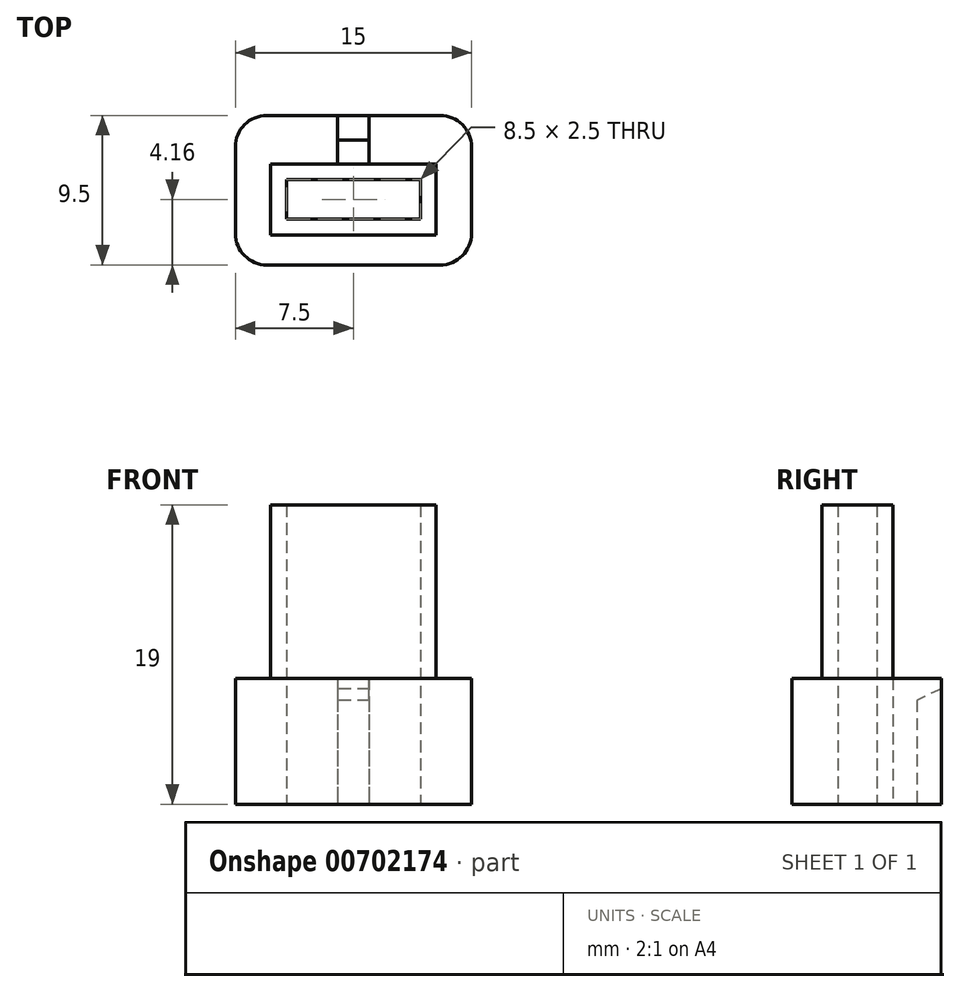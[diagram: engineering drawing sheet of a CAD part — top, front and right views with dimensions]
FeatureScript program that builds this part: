
annotation { "Feature Type Name" : "Feature", "Feature Type Description" : "" }
export const myFeature = defineFeature(function(context is Context, id is Id, definition is map)
    precondition{}
    {
        {
            var Q0;
            Q0=qCreatedBy(makeId("Top.planeOp"),FACE);
            var sketch = newSketch(context, id + "F0", { "sketchPlane" : qUnion([Q0])});
            skLineSegment(sketch, "E0.bottom", {"start": v(4.25, -1.25) * mm, "end": v(-4.25, -1.25) * mm});
            skLineSegment(sketch, "E0.top", {"start": v(4.25, 1.25) * mm, "end": v(-4.25, 1.25) * mm});
            skLineSegment(sketch, "E0.left", {"start": v(4.25, -1.25) * mm, "end": v(4.25, 1.25) * mm});
            skLineSegment(sketch, "E0.right", {"start": v(-4.25, -1.25) * mm, "end": v(-4.25, 1.25) * mm});
            skPoint(sketch, "E0.middle", {"position": v(0, 0) * mm});
            skLineSegment(sketch, "E1.bottom", {"start": v(5.25, -2.25) * mm, "end": v(-5.25, -2.25) * mm});
            skLineSegment(sketch, "E1.top", {"start": v(5.25, 2.25) * mm, "end": v(-5.25, 2.25) * mm});
            skLineSegment(sketch, "E1.left", {"start": v(5.25, -2.25) * mm, "end": v(5.25, 2.25) * mm});
            skLineSegment(sketch, "E1.right", {"start": v(-5.25, -2.25) * mm, "end": v(-5.25, 2.25) * mm});
            skLineSegment(sketch, "E2.bottom", {"start": v(1, 2.25) * mm, "end": v(-1, 2.25) * mm});
            skLineSegment(sketch, "E2.top", {"start": v(1, 3.76) * mm, "end": v(-1, 3.76) * mm});
            skLineSegment(sketch, "E2.left", {"start": v(1, 2.25) * mm, "end": v(1, 3.76) * mm});
            skLineSegment(sketch, "E2.right", {"start": v(-1, 2.25) * mm, "end": v(-1, 3.76) * mm});
            skPoint(sketch, "E2.middle", {"position": v(0, 3) * mm});
            skPoint(sketch, "E2.middle.positionSnap0", {"position": v(0, 2.25) * mm});
            skPoint(sketch, "E2.centerSnap0", {"position": v(0, 2.25) * mm});
            skLineSegment(sketch, "E3.bottom", {"start": v(7.5, -4.16) * mm, "end": v(-7.5, -4.16) * mm});
            skLineSegment(sketch, "E3.top", {"start": v(7.5, 5.34) * mm, "end": v(-7.5, 5.34) * mm});
            skLineSegment(sketch, "E3.left", {"start": v(7.5, -4.16) * mm, "end": v(7.5, 5.34) * mm});
            skLineSegment(sketch, "E3.right", {"start": v(-7.5, -4.16) * mm, "end": v(-7.5, 5.34) * mm});
            skPoint(sketch, "E3.middle", {"position": v(0, 0.59) * mm});
            skSolve(sketch);
        }
        {
            var Q0;
            Q0=makeQuery(id+"F0.imprint","IMPRINT",FACE,{"disambiguationData":[TD([[makeQuery(id+"F0.imprint","IMPRINT",EDGE,{"derivedFrom":sQuery(id+"F0.wireOp",EDGE,"E0.bottom")}),1.0]])]});
            var Q1;
            Q1=makeQuery(id+"F0.imprint","IMPRINT",FACE,{"disambiguationData":[TD([[makeQuery(id+"F0.imprint","IMPRINT",EDGE,{"derivedFrom":sQuery(id+"F0.wireOp",EDGE,"E2.bottom")}),-1.0]])]});
            extrude(context, id + "F1", {"entities" : qUnion([Q0, Q1]), "depth" : 19 * mm, "offsetDistance" : 25 * mm});
        }
        {
            var Q0;
            Q0=makeQuery(id+"F0.imprint","IMPRINT",FACE,{"disambiguationData":[TD([[makeQuery(id+"F0.imprint","IMPRINT",EDGE,{"derivedFrom":sQuery(id+"F0.wireOp",EDGE,"E1.bottom")}),1.0]])]});
            extrude(context, id + "F2", {"entities" : qUnion([Q0]), "operationType" : NewBodyOperationType.ADD, "depth" : 8 * mm, "offsetDistance" : 25 * mm});
        }
        {
            var Q0;
            Q0=makeQuery(id+"F2.opExtrude","SWEPT_EDGE",EDGE,{"disambiguationData":[OSD([sQuery(id+"F0.wireOp",EDGE,"E3.bottom"),sQuery(id+"F0.wireOp",EDGE,"E3.right")])]});
            var Q1;
            Q1=makeQuery(id+"F2.opExtrude","SWEPT_EDGE",EDGE,{"disambiguationData":[OSD([sQuery(id+"F0.wireOp",EDGE,"E3.bottom"),sQuery(id+"F0.wireOp",EDGE,"E3.left")])]});
            var Q2;
            Q2=makeQuery(id+"F2.opExtrude","SWEPT_EDGE",EDGE,{"disambiguationData":[OSD([sQuery(id+"F0.wireOp",EDGE,"E3.top"),sQuery(id+"F0.wireOp",EDGE,"E3.left")])]});
            var Q3;
            Q3=makeQuery(id+"F2.opExtrude","SWEPT_EDGE",EDGE,{"disambiguationData":[OSD([sQuery(id+"F0.wireOp",EDGE,"E3.top"),sQuery(id+"F0.wireOp",EDGE,"E3.right")])]});
            fillet(context, id + "F3", {"entities" : qUnion([Q0, Q1, Q2, Q3]), "radius" : 2 * mm, "tangentPropagation" : true, "allowEdgeOverflow" : false});
        }
        {
            var Q0;
            Q0=makeQuery(id+"F2.opExtrude","CAP_EDGE",EDGE,{"disambiguationData":[OSD([sQuery(id+"F0.wireOp",EDGE,"E2.top")])],"isStart":false});
            chamfer(context, id + "F4", {"entities" : qUnion([Q0]), "chamferType" : ChamferType.TWO_OFFSETS, "width1" : 3 * mm, "oppositeDirection" : false, "width2" : 1.4 * mm, "tangentPropagation" : true});
        }
    });
